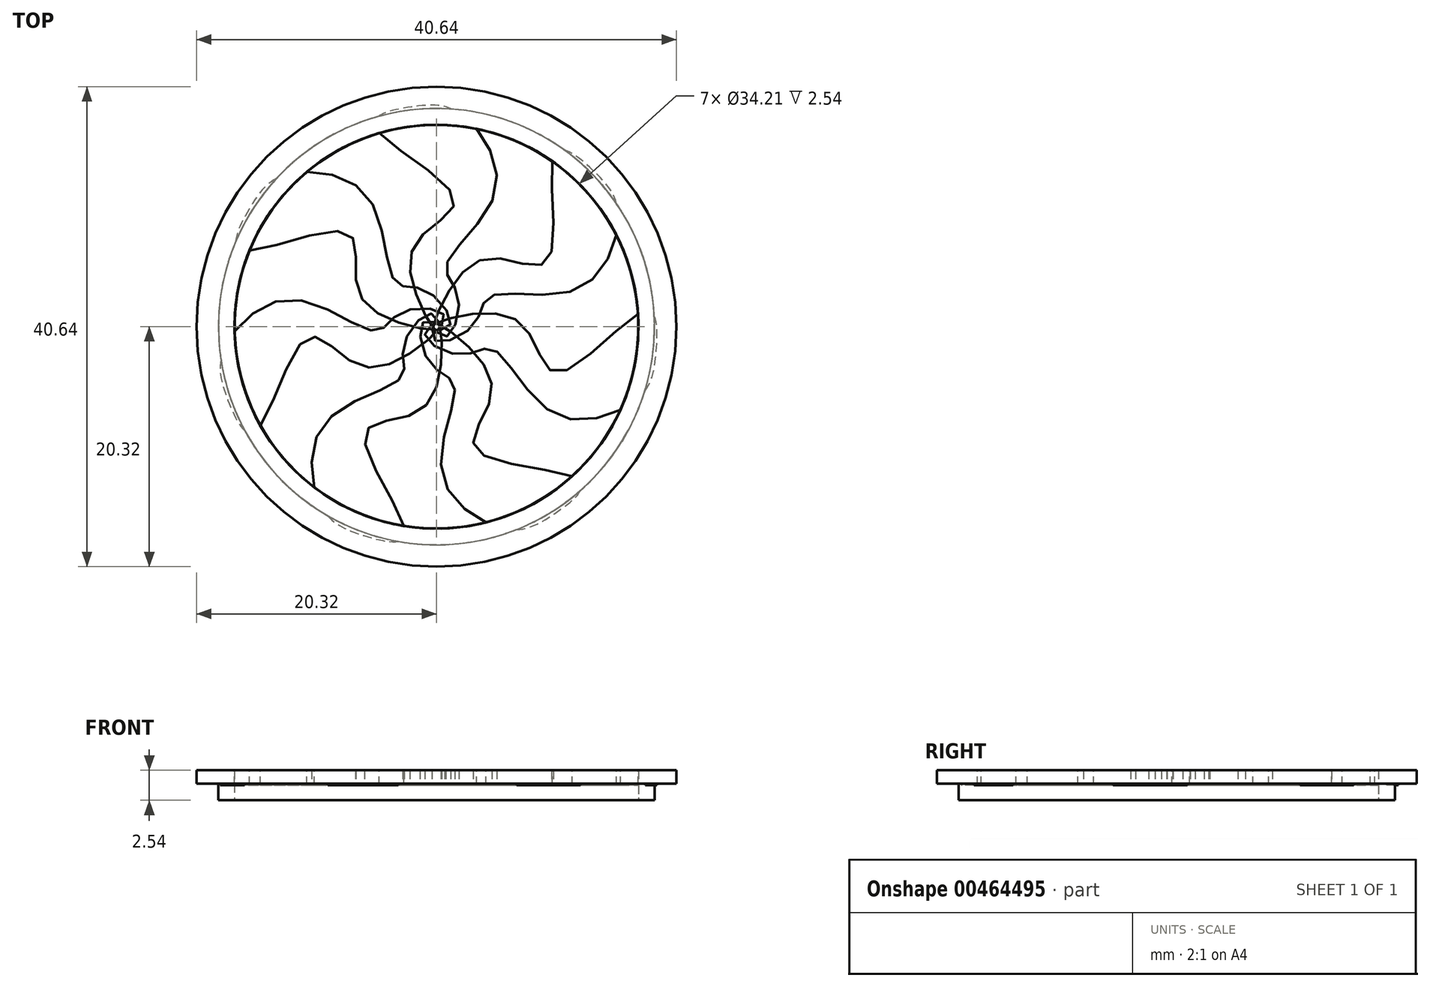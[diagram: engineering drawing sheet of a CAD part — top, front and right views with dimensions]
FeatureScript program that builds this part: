
annotation { "Feature Type Name" : "Feature", "Feature Type Description" : "" }
export const myFeature = defineFeature(function(context is Context, id is Id, definition is map)
    precondition{}
    {
        {
            var Q0;
            Q0=qCreatedBy(makeId("Front.planeOp"),FACE);
            var sketch = newSketch(context, id + "F0", { "sketchPlane" : qUnion([Q0])});
            skLineSegment(sketch, "E0.bottom", {"start": v(17.1, 0) * mm, "end": v(20.32, 0) * mm});
            skLineSegment(sketch, "E0.left", {"start": v(17.1, 0) * mm, "end": v(17.1, -2.54) * mm});
            skLineSegment(sketch, "E0.right", {"start": v(20.32, 0) * mm, "end": v(20.32, -1.13) * mm});
            skLineSegment(sketch, "E1", {"start": v(20.32, -1.13) * mm, "end": v(18.48, -1.13) * mm});
            skLineSegment(sketch, "E2", {"start": v(18.48, -1.13) * mm, "end": v(18.48, -2.54) * mm});
            skLineSegment(sketch, "E3", {"start": v(18.48, -2.54) * mm, "end": v(17.1, -2.54) * mm});
            skSolve(sketch);
        }
        {
            var Q0;
            Q0=qCreatedBy(makeId("Front.planeOp"),FACE);
            var sketch = newSketch(context, id + "F1", { "sketchPlane" : qUnion([Q0])});
            skLineSegment(sketch, "E4", {"start": v(0, -2.4) * mm, "end": v(0, 29.67) * mm});
            skSolve(sketch);
        }
        {
            var Q0;
            Q0 = qSketchRegion(id + "F0", true);
            var Q1;
            Q1=sQuery(id+"F1.wireOp",EDGE,"E4");
            revolve(context, id + "F2", {"entities" : qUnion([Q0]), "axis" : qUnion([Q1]), "revolveType" : RevolveType.FULL});
        }
        {
            var Q0;
            Q0=qCreatedBy(makeId("Top.planeOp"),FACE);
            var sketch = newSketch(context, id + "F3", { "sketchPlane" : qUnion([Q0])});
            skFitSpline(sketch, "E5", {"points": [v(-5.3, 17.09) * mm, v(1.5, 10.89) * mm, v(-1.64, 7.29) * mm, v(-1.32, 1.76) * mm, v(0.86, -0.82) * mm, v(1.83, 2.66) * mm, v(0.8, 5.1) * mm, v(4.98, 11.4) * mm, v(2.15, 17.96) * mm, v(-2, 18.63) * mm, v(-5.3, 17.09) * mm]});
            skSolve(sketch);
        }
        {
            var Q0;
            Q0=makeQuery(id+"F3.imprint","IMPRINT",FACE,{"disambiguationData":[TD([[makeQuery(id+"F3.imprint","IMPRINT",EDGE,{"derivedFrom":sQuery(id+"F3.wireOp",EDGE,"E5")}),1.0]])]});
            extrude(context, id + "F4", {"entities" : qUnion([Q0]), "operationType" : NewBodyOperationType.ADD, "oppositeDirection" : true, "depth" : 1.27 * mm});
        }
        {
            var Q0;
            Q0=makeQuery(id+"F2.opRevolve","SWEPT_BODY",BODY,{"disambiguationData":[OSD([sQuery(id+"F0.wireOp",EDGE,"E0.bottom"),sQuery(id+"F0.wireOp",EDGE,"E0.left"),sQuery(id+"F0.wireOp",EDGE,"E0.right"),sQuery(id+"F0.wireOp",EDGE,"E1"),sQuery(id+"F0.wireOp",EDGE,"E2"),sQuery(id+"F0.wireOp",EDGE,"E3")])]});
            var Q1;
            Q1=makeQuery(id+"F2.opRevolve","SWEPT_EDGE",EDGE,{"disambiguationData":[OSD([sQuery(id+"F0.wireOp",EDGE,"E0.bottom"),sQuery(id+"F0.wireOp",EDGE,"E0.right")])]});
            circularPattern(context, id + "F5", {"entities" : qUnion([Q0]), "axis" : qUnion([Q1]), "angle" : 360 * degree, "instanceCount" : 7, "equalSpace" : true});
        }
    });
